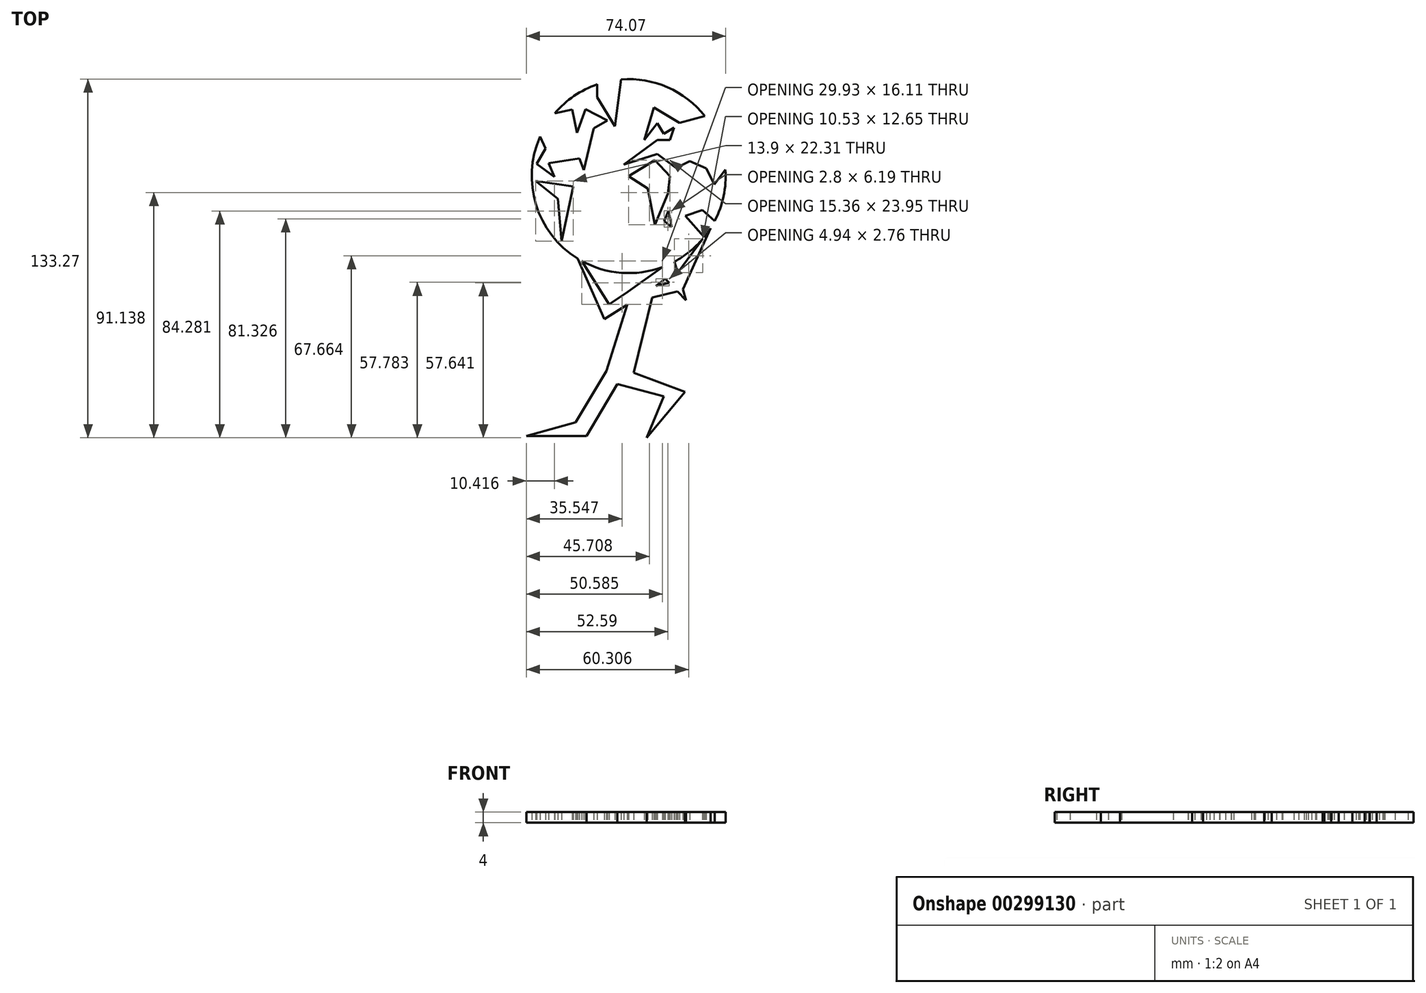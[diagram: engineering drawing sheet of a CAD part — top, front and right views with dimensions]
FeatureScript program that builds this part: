
annotation { "Feature Type Name" : "Feature", "Feature Type Description" : "" }
export const myFeature = defineFeature(function(context is Context, id is Id, definition is map)
    precondition{}
    {
        {
            var Q0;
            Q0=qCreatedBy(makeId("Top.planeOp"),FACE);
            var sketch = newSketch(context, id + "F0", { "sketchPlane" : qUnion([Q0])});
            skLineSegment(sketch, "E0", {"start": v(-28.22, -70.85) * mm, "end": v(-5.88, -70.85) * mm});
            skLineSegment(sketch, "E1", {"start": v(-5.88, -70.85) * mm, "end": v(5.53, -51.6) * mm});
            skLineSegment(sketch, "E2", {"start": v(5.53, -51.6) * mm, "end": v(22.88, -56.11) * mm});
            skLineSegment(sketch, "E3", {"start": v(22.88, -56.11) * mm, "end": v(16.46, -71.56) * mm});
            skLineSegment(sketch, "E4", {"start": v(16.46, -71.56) * mm, "end": v(30.72, -54.45) * mm});
            skLineSegment(sketch, "E5", {"start": v(30.72, -54.45) * mm, "end": v(11.7, -47.32) * mm});
            skLineSegment(sketch, "E6", {"start": v(11.7, -47.32) * mm, "end": v(18.56, -19.49) * mm});
            skLineSegment(sketch, "E7", {"start": v(18.56, -19.49) * mm, "end": v(27.93, -17.14) * mm});
            skLineSegment(sketch, "E8", {"start": v(29.92, -16.42) * mm, "end": v(40.22, 6.32) * mm});
            skLineSegment(sketch, "E9", {"start": v(24.84, -13.93) * mm, "end": v(19.9, -15.15) * mm});
            skLineSegment(sketch, "E10", {"start": v(19.9, -15.15) * mm, "end": v(23.37, -12.4) * mm});
            skLineSegment(sketch, "E11", {"start": v(23.37, -12.4) * mm, "end": v(24.84, -13.93) * mm});
            skLineSegment(sketch, "E12", {"start": v(31.15, -20.5) * mm, "end": v(29.92, -16.42) * mm});
            skLineSegment(sketch, "E13", {"start": v(26.52, -5.11) * mm, "end": v(9.52, -17.27) * mm});
            skLineSegment(sketch, "E14", {"start": v(9.52, -17.27) * mm, "end": v(2.48, -21.97) * mm});
            skLineSegment(sketch, "E15", {"start": v(2.48, -21.97) * mm, "end": v(-7.64, -5.87) * mm});
            skLineSegment(sketch, "E16", {"start": v(-9.13, -4.99) * mm, "end": v(0.72, -27.5) * mm});
            skLineSegment(sketch, "E17", {"start": v(0.72, -27.5) * mm, "end": v(9.21, -22.12) * mm});
            skLineSegment(sketch, "E18", {"start": v(9.21, -22.12) * mm, "end": v(1.53, -46.75) * mm});
            skLineSegment(sketch, "E19", {"start": v(1.53, -46.75) * mm, "end": v(-9.86, -65.84) * mm});
            skLineSegment(sketch, "E20", {"start": v(-9.86, -65.84) * mm, "end": v(-28.22, -70.85) * mm});
            skArc(sketch, "E21", {"start": v(-7.64, -5.87) * mm, "mid": v(7.08, -10.27) * mm, "end": v(22.3, -8.14) * mm});
            skLineSegment(sketch, "E22", {"start": v(19.5, 7.6) * mm, "end": v(16.94, 21.13) * mm});
            skLineSegment(sketch, "E23", {"start": v(16.94, 21.13) * mm, "end": v(9.8, 25.67) * mm});
            skLineSegment(sketch, "E24", {"start": v(9.8, 25.67) * mm, "end": v(19.5, 31.55) * mm});
            skLineSegment(sketch, "E25", {"start": v(19.5, 31.55) * mm, "end": v(25.17, 25.7) * mm});
            skLineSegment(sketch, "E26", {"start": v(25.17, 25.7) * mm, "end": v(24.43, 19.12) * mm});
            skLineSegment(sketch, "E27", {"start": v(24.43, 19.12) * mm, "end": v(19.5, 7.6) * mm});
            skLineSegment(sketch, "E28", {"start": v(22.97, 9.06) * mm, "end": v(24.6, 12.86) * mm});
            skLineSegment(sketch, "E29", {"start": v(24.6, 12.86) * mm, "end": v(25.77, 6.67) * mm});
            skLineSegment(sketch, "E30", {"start": v(25.77, 6.67) * mm, "end": v(22.97, 9.06) * mm});
            skLineSegment(sketch, "E31", {"start": v(20.41, 33.93) * mm, "end": v(27.36, 28.63) * mm});
            skPoint(sketch, "E31.endSnap0", {"position": v(22.33, 28.63) * mm});
            skLineSegment(sketch, "E32", {"start": v(27.36, 28.63) * mm, "end": v(32.48, 31.19) * mm});
            skLineSegment(sketch, "E33", {"start": v(32.48, 31.19) * mm, "end": v(38.55, 28.59) * mm});
            skLineSegment(sketch, "E34", {"start": v(38.55, 28.59) * mm, "end": v(41.62, 22.6) * mm});
            skLineSegment(sketch, "E35", {"start": v(41.62, 22.6) * mm, "end": v(45.77, 28.03) * mm});
            skLineSegment(sketch, "E36", {"start": v(20.41, 33.93) * mm, "end": v(7.98, 29.9) * mm});
            skLineSegment(sketch, "E37", {"start": v(7.98, 29.9) * mm, "end": v(20.41, 39.05) * mm});
            skLineSegment(sketch, "E38", {"start": v(20.41, 39.05) * mm, "end": v(25.17, 39.05) * mm});
            skLineSegment(sketch, "E39", {"start": v(25.17, 39.05) * mm, "end": v(26.63, 43.62) * mm});
            skLineSegment(sketch, "E40", {"start": v(26.63, 43.62) * mm, "end": v(22.79, 41.34) * mm});
            skPoint(sketch, "E40.endSnap0", {"position": v(25.9, 41.34) * mm});
            skLineSegment(sketch, "E41", {"start": v(22.79, 41.34) * mm, "end": v(20.41, 45.33) * mm});
            skLineSegment(sketch, "E42", {"start": v(20.41, 45.33) * mm, "end": v(15.66, 39.05) * mm});
            skLineSegment(sketch, "E43", {"start": v(15.66, 39.05) * mm, "end": v(19.13, 51.12) * mm});
            skLineSegment(sketch, "E44", {"start": v(19.13, 51.12) * mm, "end": v(28.64, 45.45) * mm});
            skLineSegment(sketch, "E45", {"start": v(28.64, 45.45) * mm, "end": v(38.11, 47.98) * mm});
            skLineSegment(sketch, "E46", {"start": v(-24.75, 23.87) * mm, "end": v(-10.86, 21.86) * mm});
            skLineSegment(sketch, "E47", {"start": v(-10.86, 21.86) * mm, "end": v(-15.06, 1.57) * mm});
            skLineSegment(sketch, "E48", {"start": v(-15.06, 1.57) * mm, "end": v(-16.52, 17.3) * mm});
            skLineSegment(sketch, "E49", {"start": v(-16.52, 17.3) * mm, "end": v(-24.75, 23.87) * mm});
            skLineSegment(sketch, "E50", {"start": v(-17.8, 25.34) * mm, "end": v(-20, 30.46) * mm});
            skPoint(sketch, "E50.startSnap0", {"position": v(-17.8, 22.87) * mm});
            skLineSegment(sketch, "E51", {"start": v(-20, 30.46) * mm, "end": v(-8.48, 32.29) * mm});
            skLineSegment(sketch, "E52", {"start": v(-8.48, 32.29) * mm, "end": v(-6.83, 27.9) * mm});
            skLineSegment(sketch, "E53", {"start": v(-6.83, 27.9) * mm, "end": v(-3.18, 43.44) * mm});
            skLineSegment(sketch, "E54", {"start": v(-3.18, 43.44) * mm, "end": v(1.94, 46.37) * mm});
            skLineSegment(sketch, "E55", {"start": v(1.94, 46.37) * mm, "end": v(-6.28, 50.57) * mm});
            skLineSegment(sketch, "E56", {"start": v(-6.28, 50.57) * mm, "end": v(-9.4, 41.8) * mm});
            skLineSegment(sketch, "E57", {"start": v(-9.4, 41.8) * mm, "end": v(-11.22, 50.39) * mm});
            skLineSegment(sketch, "E58", {"start": v(-11.22, 50.39) * mm, "end": v(-17.64, 49.02) * mm});
            skLineSegment(sketch, "E59", {"start": v(-23.08, 40.4) * mm, "end": v(-21.1, 35.94) * mm});
            skLineSegment(sketch, "E60", {"start": v(-21.1, 35.94) * mm, "end": v(-24.39, 30.27) * mm});
            skLineSegment(sketch, "E61", {"start": v(-24.39, 30.27) * mm, "end": v(-17.8, 25.34) * mm});
            skLineSegment(sketch, "E62", {"start": v(-1.9, 59.75) * mm, "end": v(-1.9, 54.96) * mm});
            skLineSegment(sketch, "E63", {"start": v(-1.9, 54.96) * mm, "end": v(4.69, 44.17) * mm});
            skLineSegment(sketch, "E64", {"start": v(4.69, 44.17) * mm, "end": v(7.04, 61.6) * mm});
            skLineSegment(sketch, "E65", {"start": v(41.8, 9.06) * mm, "end": v(37.23, 13.09) * mm});
            skLineSegment(sketch, "E66", {"start": v(37.23, 13.09) * mm, "end": v(30.83, 10.9) * mm});
            skLineSegment(sketch, "E67", {"start": v(30.83, 10.9) * mm, "end": v(37.85, 3.02) * mm});
            skLineSegment(sketch, "E68.trimOffspring", {"start": v(27.93, -17.14) * mm, "end": v(31.15, -20.5) * mm});
            skLineSegment(sketch, "E69.trimOffspring", {"start": v(28.06, -10.22) * mm, "end": v(26.52, -5.11) * mm});
            skArc(sketch, "E70.trimOffspring", {"start": v(37.85, 3.02) * mm, "mid": v(39.08, 4.64) * mm, "end": v(40.22, 6.32) * mm});
            skLineSegment(sketch, "E71.trimOffspring", {"start": v(37.35, 2.43) * mm, "end": v(28.06, -10.22) * mm});
            skArc(sketch, "E72.trimOffspring", {"start": v(41.8, 9.06) * mm, "mid": v(45.08, 18.28) * mm, "end": v(45.77, 28.03) * mm});
            skArc(sketch, "E73.trimOffspring", {"start": v(-23.08, 40.4) * mm, "mid": v(-24.64, 15.08) * mm, "end": v(-9.13, -4.99) * mm});
            skArc(sketch, "E74.trimOffspring", {"start": v(-1.9, 59.75) * mm, "mid": v(-10.5, 55.45) * mm, "end": v(-17.64, 49.02) * mm});
            skArc(sketch, "E75.trimOffspring", {"start": v(38.11, 47.98) * mm, "mid": v(24.28, 58.68) * mm, "end": v(7.04, 61.6) * mm});
            skArc(sketch, "E76.trimOffspring", {"start": v(26.82, -6.1) * mm, "mid": v(32.5, -2.34) * mm, "end": v(37.35, 2.43) * mm});
            skSolve(sketch);
        }
        {
            var Q0;
            Q0 = qSketchRegion(id + "F0", true);
            extrude(context, id + "F1", {"entities" : qUnion([Q0]), "depth" : 4 * mm, "offsetDistance" : 25.4 * mm});
        }
    });
